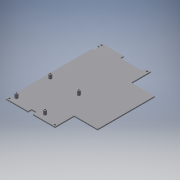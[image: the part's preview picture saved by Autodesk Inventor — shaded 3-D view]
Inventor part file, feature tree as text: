
AUTODESK INVENTOR PART (.ipt)
format: ipt  version: 2016 (Build 200138000, 138)  size: 199,168 bytes
history: native  units: in
note: dims shown in document units (in); Inventor stores cm internally (conversion verified against a paired STEP export)
features: extrude x5, sketch x4
ambient origin geometry x8: Origin, YZ Plane, XZ Plane, XY Plane, X Axis, Y Axis, Z Axis, Center Point
bodies: Body1 (feature_tree)
feature tree (9):
  extrude  "Extrusion2"  Depth=0.0394in
  extrude  "Extrusion3"  TaperAngle=0.0deg  [1 undecoded]
  extrude  "Extrusion4"  Depth=0.0787in TaperAngle=0.0deg
  extrude  "Extrusion7"  Depth=0.5906in
  extrude  "Extrusion8"  Depth=0.5906in
  sketch  "Sketch1"  dims[d0=0.0394in d4=0.0394in d5=0.0394in d6=0.0394in d7=0.0394in d8=0.0394in d10=0.0394in d11=0.0394in d12=0.0394in d13=0.0394in d14=0.0394in d15=0.0394in]
  sketch  "Sketch2"  dims[d16=0.2362in d17=0.0in]
  sketch  "Sketch3"  dims[d18=0.0in d21=0.0787in d22=0.0in]
  sketch  "Sketch6"  dims[d25=0.0394in d26=0.1181in d27=0.1181in d28=0.1181in d29=0.3937in d30=0.0in d31=1.9291in d32=2.2835in d33=1.9291in d34=2.2835in d35=0.3937in d36=0.3937in d37=0.315in d38=0.315in d39=0.2756in d40=0.0in d63=0.2756in d64=0.1575in d65=0.3543in d66=0.2756in d67=0.3543in d68=0.3937in d69=0.0in d70=0.1969in d71=0.1969in d72=0.1969in d73=0.1969in d75=6.4567in d76=6.4567in d77=6.5354in d79=1.2992in d82=1.2992in d83=0.1575in d92=0.3937in d93=0.0in d94=0.5906in]
note: 1 required parameter value undecoded (feature->parameter linkage not recoverable at this tier; creation-order binding heuristic only, values carry confidence <= 0.55)
